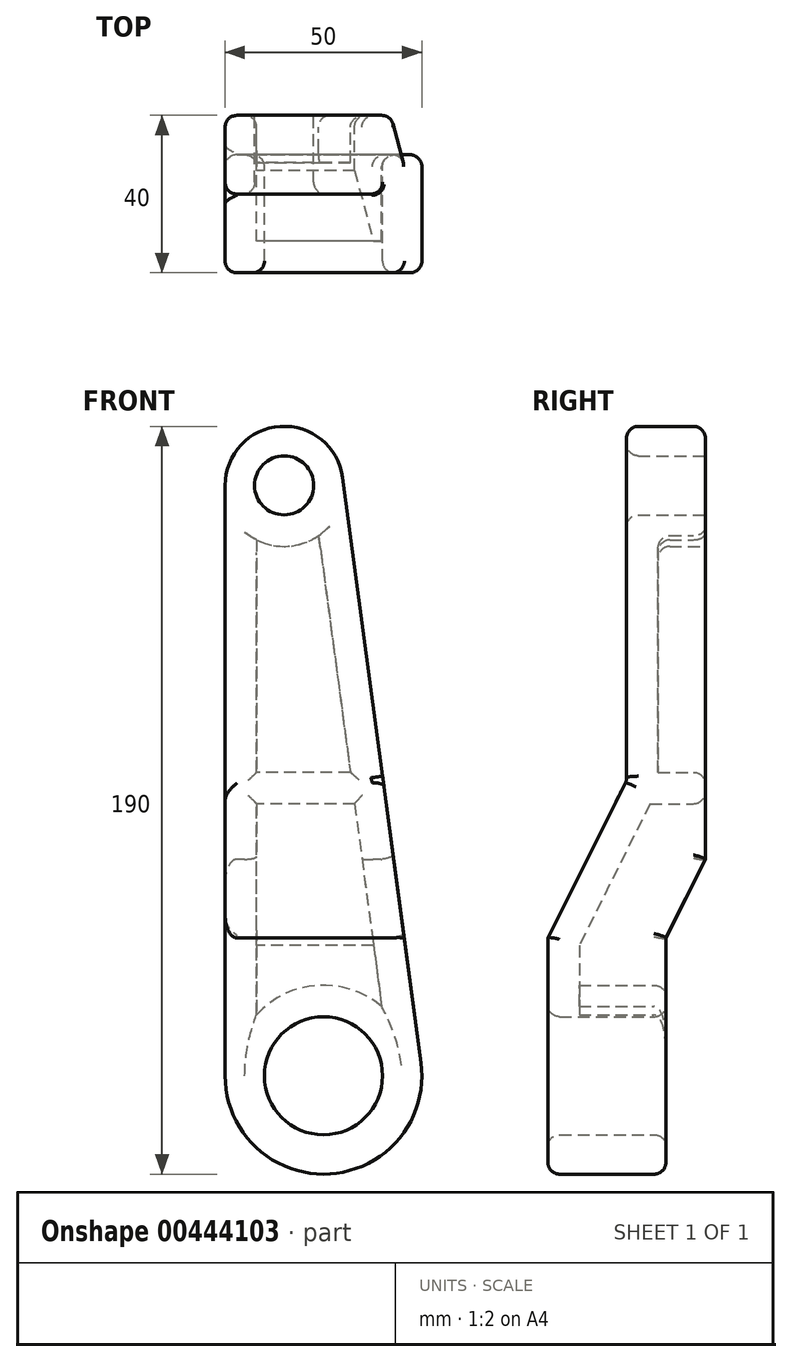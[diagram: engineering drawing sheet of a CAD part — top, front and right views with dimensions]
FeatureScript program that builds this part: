
annotation { "Feature Type Name" : "Feature", "Feature Type Description" : "" }
export const myFeature = defineFeature(function(context is Context, id is Id, definition is map)
    precondition{}
    {
        {
            var Q0;
            Q0=qCreatedBy(makeId("Front.planeOp"),FACE);
            var sketch = newSketch(context, id + "F0", { "sketchPlane" : qUnion([Q0])});
            skArc(sketch, "E0", {"start": v(-25, 0) * mm, "mid": v(1.66, -24.94) * mm, "end": v(24.78, 3.32) * mm});
            skArc(sketch, "E1", {"start": v(4.87, 152) * mm, "mid": v(-11, 164.97) * mm, "end": v(-25, 150) * mm});
            skLineSegment(sketch, "E2", {"start": v(4.87, 152) * mm, "end": v(24.78, 3.32) * mm});
            skLineSegment(sketch, "E3", {"start": v(-25, 150) * mm, "end": v(-25, 0) * mm});
            skSolve(sketch);
        }
        {
            var Q0;
            Q0=qSketchRegion(id+"F0",true);
            extrude(context, id + "F1", {"entities" : qUnion([Q0]), "depth" : 40 * mm});
        }
        {
            var Q0;
            Q0=makeQuery(id+"F1.opExtrude","SWEPT_FACE",FACE,{"disambiguationData":[OSD([sQuery(id+"F0.wireOp",EDGE,"E3")])]});
            var sketch = newSketch(context, id + "F2", { "sketchPlane" : qUnion([Q0])});
            skLineSegment(sketch, "E4", {"start": v(0, 0) * mm, "end": v(0, 55) * mm});
            skLineSegment(sketch, "E5", {"start": v(0, 55) * mm, "end": v(0, -25.94) * mm});
            skLineSegment(sketch, "E6", {"start": v(10, -25.94) * mm, "end": v(10, 35) * mm});
            skLineSegment(sketch, "E7", {"start": v(10, 35) * mm, "end": v(0, 55) * mm});
            skLineSegment(sketch, "E8", {"start": v(40, 35) * mm, "end": v(20, 75) * mm});
            skLineSegment(sketch, "E9", {"start": v(20, 75) * mm, "end": v(20, 165.94) * mm});
            skLineSegment(sketch, "E10", {"start": v(40, 165.97) * mm, "end": v(40, 35) * mm});
            skLineSegment(sketch, "E11", {"start": v(10, -25.94) * mm, "end": v(0, -25.94) * mm});
            skLineSegment(sketch, "E12", {"start": v(40, 165.97) * mm, "end": v(20, 165.94) * mm});
            skSolve(sketch);
        }
        {
            var Q0;
            Q0=qSketchRegion(id+"F2",true);
            extrude(context, id + "F3", {"entities" : qUnion([Q0]), "operationType" : NewBodyOperationType.REMOVE, "endBound" : BoundingType.THROUGH_ALL, "oppositeDirection" : true, "depth" : 25 * mm});
        }
        {
            var Q0;
            Q0=makeQuery(id+"F1.opExtrude","CAP_FACE",FACE,{"disambiguationData":[OSD([sQuery(id+"F0.wireOp",EDGE,"E0"),sQuery(id+"F0.wireOp",EDGE,"E1"),sQuery(id+"F0.wireOp",EDGE,"E2"),sQuery(id+"F0.wireOp",EDGE,"E3")])],"isStart":true});
            var sketch = newSketch(context, id + "F4", { "sketchPlane" : qUnion([Q0])});
            skCircle(sketch, "E13", {"center": v(0, 0) * mm, "radius": 15 * mm});
            skCircle(sketch, "E14", {"center": v(10, 150) * mm, "radius": 7.5 * mm});
            skSolve(sketch);
        }
        {
            var Q0;
            Q0=qSketchRegion(id+"F4",true);
            extrude(context, id + "F5", {"entities" : qUnion([Q0]), "operationType" : NewBodyOperationType.REMOVE, "endBound" : BoundingType.THROUGH_ALL, "oppositeDirection" : true, "depth" : 25 * mm});
        }
        {
            var Q0;
            Q0=makeQuery(id+"F1.opExtrude","CAP_FACE",FACE,{"disambiguationData":[OSD([sQuery(id+"F0.wireOp",EDGE,"E0"),sQuery(id+"F0.wireOp",EDGE,"E1"),sQuery(id+"F0.wireOp",EDGE,"E2"),sQuery(id+"F0.wireOp",EDGE,"E3")])],"isStart":true});
            var Q1;
            Q1=makeQuery(id+"F3.boolean.opBoolean","COPY",FACE,{"derivedFrom":makeQuery(id+"F3.opExtrude","SWEPT_FACE",FACE,{"disambiguationData":[OSD([sQuery(id+"F2.wireOp",EDGE,"E7")])]})});
            var Q2;
            Q2=makeQuery(id+"F3.boolean.opBoolean","COPY",FACE,{"derivedFrom":makeQuery(id+"F3.opExtrude","SWEPT_FACE",FACE,{"disambiguationData":[OSD([sQuery(id+"F2.wireOp",EDGE,"E6")])]})});
            shell(context, id + "F6", {"entities" : qUnion([Q0, Q1, Q2]), "thickness" : 8 * mm});
        }
        {
            var Q0;
            Q0=makeQuery(id+"F1.opExtrude","CAP_FACE",FACE,{"disambiguationData":[OSD([sQuery(id+"F0.wireOp",EDGE,"E0"),sQuery(id+"F0.wireOp",EDGE,"E1"),sQuery(id+"F0.wireOp",EDGE,"E2"),sQuery(id+"F0.wireOp",EDGE,"E3")])],"isStart":true});
            var sketch = newSketch(context, id + "F7", { "sketchPlane" : qUnion([Q0])});
            skLineSegment(sketch, "E15", {"start": v(-6.82, 77.11) * mm, "end": v(17, 77.11) * mm});
            skLineSegment(sketch, "E16", {"start": v(-7.9, 69.11) * mm, "end": v(17, 69.11) * mm});
            skLineSegment(sketch, "E17.0", {"start": v(1.23, 137.22) * mm, "end": v(-9.79, 55) * mm});
            skLineSegment(sketch, "E18.0", {"start": v(17, 136.17) * mm, "end": v(17, 55) * mm});
            skSolve(sketch);
        }
        {
            var Q0;
            Q0 = qSketchRegion(id + "F7", true);
            extrude(context, id + "F8", {"entities" : qUnion([Q0]), "operationType" : NewBodyOperationType.ADD, "endBound" : BoundingType.UP_TO_NEXT, "oppositeDirection" : true, "depth" : 25 * mm});
        }
        {
            var Q0;
            Q0=makeQuery(id+"F3.boolean.opBoolean","INTERSECT",EDGE,{"derivedFrom":[makeQuery(id+"F1.opExtrude","SWEPT_FACE",FACE,{"disambiguationData":[OSD([sQuery(id+"F0.wireOp",EDGE,"E2")])]}),makeQuery(id+"F3.opExtrude","SWEPT_FACE",FACE,{"disambiguationData":[OSD([sQuery(id+"F2.wireOp",EDGE,"E9")])]})]});
            var Q1;
            Q1=makeQuery(id+"F3.boolean.opBoolean","INTERSECT",EDGE,{"derivedFrom":[makeQuery(id+"F1.opExtrude","SWEPT_FACE",FACE,{"disambiguationData":[OSD([sQuery(id+"F0.wireOp",EDGE,"E2")])]}),makeQuery(id+"F3.opExtrude","SWEPT_FACE",FACE,{"disambiguationData":[OSD([sQuery(id+"F2.wireOp",EDGE,"E8")])]})]});
            var Q2;
            Q2=makeQuery(id+"F1.opExtrude","CAP_EDGE",EDGE,{"disambiguationData":[OSD([sQuery(id+"F0.wireOp",EDGE,"E2")])],"isStart":false});
            var Q3;
            Q3=makeQuery(id+"F3.boolean.opBoolean","COPY",EDGE,{"derivedFrom":makeQuery(id+"F3.opExtrude","CAP_EDGE",EDGE,{"disambiguationData":[OSD([sQuery(id+"F2.wireOp",EDGE,"E8")])],"isStart":true})});
            var Q4;
            Q4=makeQuery(id+"F1.opExtrude","CAP_EDGE",EDGE,{"disambiguationData":[OSD([sQuery(id+"F0.wireOp",EDGE,"E2")])],"isStart":true});
            var Q5;
            Q5=makeQuery(id+"F3.boolean.opBoolean","COPY",EDGE,{"derivedFrom":makeQuery(id+"F3.opExtrude","CAP_EDGE",EDGE,{"disambiguationData":[OSD([sQuery(id+"F2.wireOp",EDGE,"E7")])],"isStart":true})});
            var Q6;
            Q6=makeQuery(id+"F3.boolean.opBoolean","COPY",EDGE,{"derivedFrom":makeQuery(id+"F3.opExtrude","CAP_EDGE",EDGE,{"disambiguationData":[OSD([sQuery(id+"F2.wireOp",EDGE,"E6")])],"isStart":true})});
            var Q7;
            Q7=makeQuery(id+"F3.boolean.opBoolean","INTERSECT",EDGE,{"derivedFrom":[makeQuery(id+"F1.opExtrude","SWEPT_FACE",FACE,{"disambiguationData":[OSD([sQuery(id+"F0.wireOp",EDGE,"E2")])]}),makeQuery(id+"F3.opExtrude","SWEPT_FACE",FACE,{"disambiguationData":[OSD([sQuery(id+"F2.wireOp",EDGE,"E7")])]})]});
            var Q8;
            Q8=makeQuery(id+"F3.boolean.opBoolean","INTERSECT",EDGE,{"derivedFrom":[makeQuery(id+"F1.opExtrude","SWEPT_FACE",FACE,{"disambiguationData":[OSD([sQuery(id+"F0.wireOp",EDGE,"E1")])]}),makeQuery(id+"F3.opExtrude","SWEPT_FACE",FACE,{"disambiguationData":[OSD([sQuery(id+"F2.wireOp",EDGE,"E9")])]})]});
            var Q9;
            Q9=makeQuery(id+"F3.boolean.opBoolean","COPY",EDGE,{"derivedFrom":makeQuery(id+"F3.opExtrude","CAP_EDGE",EDGE,{"disambiguationData":[OSD([sQuery(id+"F2.wireOp",EDGE,"E9")])],"isStart":true})});
            var Q10;
            Q10=makeQuery(id+"F1.opExtrude","CAP_EDGE",EDGE,{"disambiguationData":[OSD([sQuery(id+"F0.wireOp",EDGE,"E3")])],"isStart":false});
            var Q11;
            Q11=makeQuery(id+"F1.opExtrude","CAP_EDGE",EDGE,{"disambiguationData":[OSD([sQuery(id+"F0.wireOp",EDGE,"E0")])],"isStart":false});
            var Q12;
            Q12=makeQuery(id+"F1.opExtrude","CAP_EDGE",EDGE,{"disambiguationData":[OSD([sQuery(id+"F0.wireOp",EDGE,"E3")])],"isStart":true});
            var Q13;
            Q13=makeQuery(id+"F1.opExtrude","CAP_EDGE",EDGE,{"disambiguationData":[OSD([sQuery(id+"F0.wireOp",EDGE,"E1")])],"isStart":true});
            var Q14;
            Q14=makeQuery(id+"F3.boolean.opBoolean","INTERSECT",EDGE,{"derivedFrom":[makeQuery(id+"F1.opExtrude","SWEPT_FACE",FACE,{"disambiguationData":[OSD([sQuery(id+"F0.wireOp",EDGE,"E2")])]}),makeQuery(id+"F3.opExtrude","SWEPT_FACE",FACE,{"disambiguationData":[OSD([sQuery(id+"F2.wireOp",EDGE,"E6")])]})]});
            var Q15;
            Q15=makeQuery(id+"F3.boolean.opBoolean","INTERSECT",EDGE,{"derivedFrom":[makeQuery(id+"F1.opExtrude","SWEPT_FACE",FACE,{"disambiguationData":[OSD([sQuery(id+"F0.wireOp",EDGE,"E0")])]}),makeQuery(id+"F3.opExtrude","SWEPT_FACE",FACE,{"disambiguationData":[OSD([sQuery(id+"F2.wireOp",EDGE,"E6")])]})]});
            var Q16;
            Q16=makeQuery(id+"F3.boolean.opBoolean","COPY",EDGE,{"derivedFrom":makeQuery(id+"F3.opExtrude","SWEPT_EDGE",EDGE,{"disambiguationData":[OSD([sQuery(id+"F2.wireOp",EDGE,"E8"),sQuery(id+"F2.wireOp",EDGE,"E9")])]})});
            var Q17;
            Q17=makeQuery(id+"F3.boolean.opBoolean","COPY",EDGE,{"derivedFrom":makeQuery(id+"F3.opExtrude","SWEPT_EDGE",EDGE,{"disambiguationData":[OSD([sQuery(id+"F0.wireOp",EDGE,"E3"),sQuery(id+"F2.wireOp",EDGE,"E8"),sQuery(id+"F2.wireOp",EDGE,"E10")])]})});
            var Q18;
            Q18=makeQuery(id+"F5.boolean.opBoolean","INTERSECT",EDGE,{"derivedFrom":[makeQuery(id+"F3.boolean.opBoolean","COPY",FACE,{"derivedFrom":makeQuery(id+"F3.opExtrude","SWEPT_FACE",FACE,{"disambiguationData":[OSD([sQuery(id+"F2.wireOp",EDGE,"E9")])]})}),makeQuery(id+"F5.opExtrude","SWEPT_FACE",FACE,{"disambiguationData":[OSD([sQuery(id+"F4.wireOp",EDGE,"E14")])]})]});
            var Q19;
            Q19=makeQuery(id+"F5.boolean.opBoolean","COPY",EDGE,{"derivedFrom":makeQuery(id+"F5.opExtrude","CAP_EDGE",EDGE,{"disambiguationData":[OSD([sQuery(id+"F4.wireOp",EDGE,"E14")])],"isStart":true})});
            var Q20;
            {var subQ0=sQuery(id+"F0.wireOp",EDGE,"E2");Q20=makeQuery(id+"F8.boolean.opBoolean","SPLIT",EDGE,{"disambiguationData":[TD([makeQuery(id+"F6.opShell","OFFSET_FACE",FACE,{"disambiguationData":[OSD([sQuery(id+"F4.wireOp",EDGE,"E14")])]})])],"derivedFrom":makeQuery(id+"F6.opShell","OFFSET_EDGE",EDGE,{"disambiguationData":[OSD([subQ0]),TDD([makeQuery(id+"F1.opExtrude","CAP_EDGE",EDGE,{"disambiguationData":[OSD([subQ0])],"isStart":true})])]})});}
            var Q21;
            Q21=makeQuery(id+"F6.opShell","OFFSET_EDGE",EDGE,{"disambiguationData":[OSD([sQuery(id+"F4.wireOp",EDGE,"E14")])]});
            var Q22;
            {var subQ0=sQuery(id+"F0.wireOp",EDGE,"E3");Q22=makeQuery(id+"F8.boolean.opBoolean","SPLIT",EDGE,{"disambiguationData":[TD([makeQuery(id+"F6.opShell","OFFSET_FACE",FACE,{"disambiguationData":[OSD([sQuery(id+"F4.wireOp",EDGE,"E14")])]})])],"derivedFrom":makeQuery(id+"F6.opShell","OFFSET_EDGE",EDGE,{"disambiguationData":[OSD([subQ0]),TDD([makeQuery(id+"F1.opExtrude","CAP_EDGE",EDGE,{"disambiguationData":[OSD([subQ0])],"isStart":true})])]})});}
            var Q23;
            Q23=makeQuery(id+"F8.opExtrude","CAP_EDGE",EDGE,{"disambiguationData":[OSD([sQuery(id+"F7.wireOp",EDGE,"E15")])],"isStart":true});
            var Q24;
            Q24=makeQuery(id+"F5.boolean.opBoolean","INTERSECT",EDGE,{"derivedFrom":[makeQuery(id+"F3.boolean.opBoolean","COPY",FACE,{"derivedFrom":makeQuery(id+"F3.opExtrude","SWEPT_FACE",FACE,{"disambiguationData":[OSD([sQuery(id+"F2.wireOp",EDGE,"E6")])]})}),makeQuery(id+"F5.opExtrude","SWEPT_FACE",FACE,{"disambiguationData":[OSD([sQuery(id+"F4.wireOp",EDGE,"E13")])]})]});
            var Q25;
            Q25=makeQuery(id+"F6.opShell","OFFSET_EDGE",EDGE,{"disambiguationData":[OSD([sQuery(id+"F0.wireOp",EDGE,"E2"),sQuery(id+"F2.wireOp",EDGE,"E7")])]});
            var Q26;
            {var subQ1=sQuery(id+"F0.wireOp",EDGE,"E2");Q26=makeQuery(id+"F8.boolean.opBoolean","SPLIT",EDGE,{"disambiguationData":[TD([makeQuery(id+"F6.opShell","OFFSET_FACE",FACE,{"disambiguationData":[OSD([sQuery(id+"F2.wireOp",EDGE,"E7")])]})])],"derivedFrom":makeQuery(id+"F6.opShell","OFFSET_EDGE",EDGE,{"disambiguationData":[OSD([subQ1]),TDD([makeQuery(id+"F1.opExtrude","CAP_EDGE",EDGE,{"disambiguationData":[OSD([subQ1])],"isStart":true})])]})});}
            var Q27;
            Q27=makeQuery(id+"F8.opExtrude","CAP_EDGE",EDGE,{"disambiguationData":[OSD([sQuery(id+"F7.wireOp",EDGE,"E16")])],"isStart":true});
            var Q28;
            Q28=makeQuery(id+"F6.opShell","OFFSET_EDGE",EDGE,{"disambiguationData":[OSD([sQuery(id+"F0.wireOp",EDGE,"E2"),sQuery(id+"F2.wireOp",EDGE,"E6")])]});
            var Q29;
            Q29=makeQuery(id+"F6.opShell","OFFSET_EDGE",EDGE,{"disambiguationData":[OSD([sQuery(id+"F2.wireOp",EDGE,"E6"),sQuery(id+"F4.wireOp",EDGE,"E13")])]});
            var Q30;
            Q30=makeQuery(id+"F6.opShell","OFFSET_EDGE",EDGE,{"disambiguationData":[OSD([sQuery(id+"F2.wireOp",EDGE,"E6")])]});
            var Q31;
            Q31=makeQuery(id+"F6.opShell","OFFSET_EDGE",EDGE,{"disambiguationData":[OSD([sQuery(id+"F2.wireOp",EDGE,"E7")])]});
            var Q32;
            {var subQ0=sQuery(id+"F0.wireOp",EDGE,"E3");Q32=makeQuery(id+"F8.boolean.opBoolean","SPLIT",EDGE,{"disambiguationData":[TD([makeQuery(id+"F3.boolean.opBoolean","COPY",FACE,{"derivedFrom":makeQuery(id+"F3.opExtrude","SWEPT_FACE",FACE,{"disambiguationData":[OSD([sQuery(id+"F2.wireOp",EDGE,"E7")])]})})])],"derivedFrom":makeQuery(id+"F6.opShell","OFFSET_EDGE",EDGE,{"disambiguationData":[OSD([subQ0]),TDD([makeQuery(id+"F1.opExtrude","CAP_EDGE",EDGE,{"disambiguationData":[OSD([subQ0])],"isStart":true})])]})});}
            var Q33;
            Q33=makeQuery(id+"F5.boolean.opBoolean","INTERSECT",EDGE,{"derivedFrom":[makeQuery(id+"F1.opExtrude","CAP_FACE",FACE,{"disambiguationData":[OSD([sQuery(id+"F0.wireOp",EDGE,"E0"),sQuery(id+"F0.wireOp",EDGE,"E1"),sQuery(id+"F0.wireOp",EDGE,"E2"),sQuery(id+"F0.wireOp",EDGE,"E3")])],"isStart":false}),makeQuery(id+"F5.opExtrude","SWEPT_FACE",FACE,{"disambiguationData":[OSD([sQuery(id+"F4.wireOp",EDGE,"E13")])]})]});
            fillet(context, id + "F9", {"entities" : qUnion([Q0, Q1, Q2, Q3, Q4, Q5, Q6, Q7, Q8, Q9, Q10, Q11, Q12, Q13, Q14, Q15, Q16, Q17, Q18, Q19, Q20, Q21, Q22, Q23, Q24, Q25, Q26, Q27, Q28, Q29, Q30, Q31, Q32, Q33]), "radius" : 3 * mm, "tangentPropagation" : true, "allowEdgeOverflow" : false});
        }
    });
